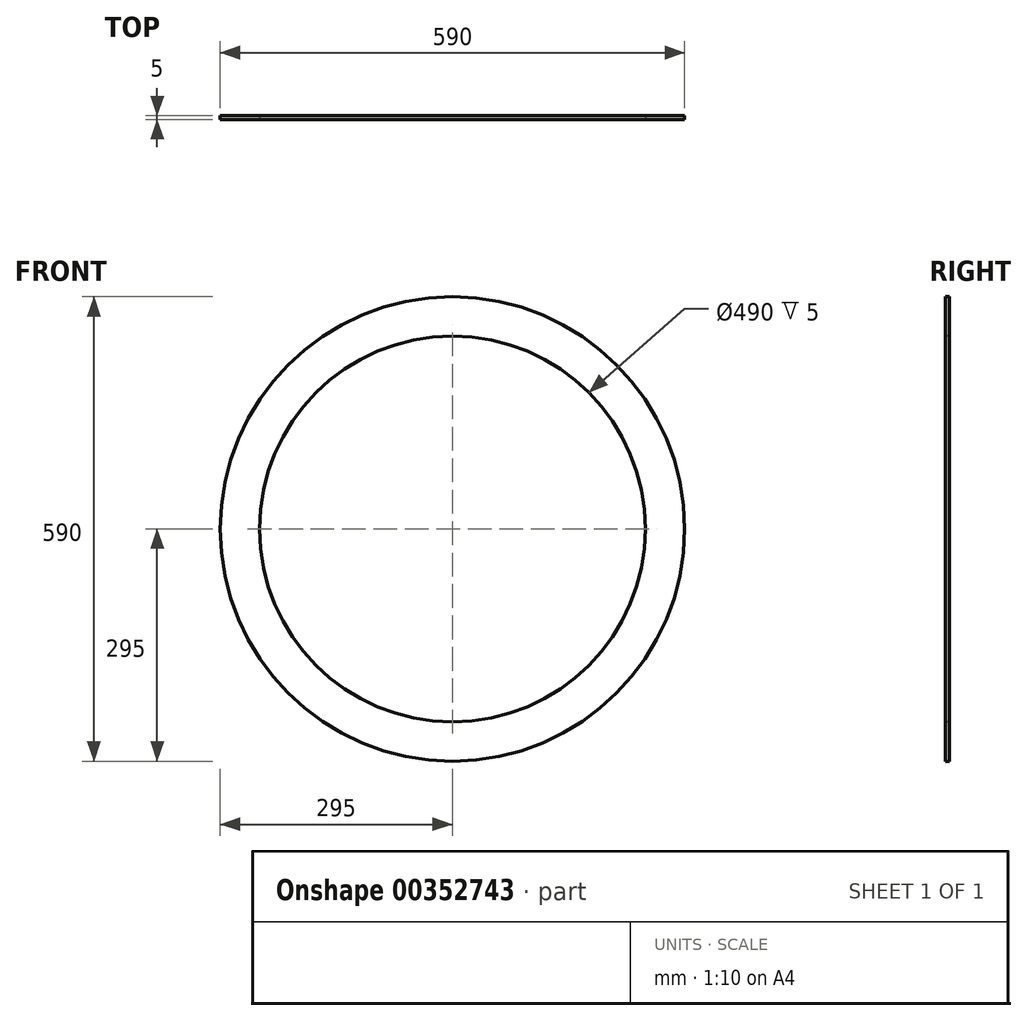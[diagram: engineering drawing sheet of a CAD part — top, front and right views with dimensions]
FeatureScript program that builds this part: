
annotation { "Feature Type Name" : "Feature", "Feature Type Description" : "" }
export const myFeature = defineFeature(function(context is Context, id is Id, definition is map)
    precondition{}
    {
        {
            var Q0;
            Q0=qCreatedBy(makeId("Front.planeOp"),FACE);
            var sketch = newSketch(context, id + "F0", { "sketchPlane" : qUnion([Q0])});
            skCircle(sketch, "E0", {"center": v(0, 0) * mm, "radius": 245 * mm});
            skCircle(sketch, "E1", {"center": v(0, 0) * mm, "radius": 295 * mm});
            skSolve(sketch);
        }
        {
            var Q0;
            Q0=makeQuery(id+"F0.imprint","IMPRINT",FACE,{"disambiguationData":[TD([[makeQuery(id+"F0.imprint","IMPRINT",EDGE,{"derivedFrom":sQuery(id+"F0.wireOp",EDGE,"E0")}),-1.0]])]});
            extrude(context, id + "F1", {"entities" : qUnion([Q0]), "oppositeDirection" : true, "depth" : 5 * mm});
        }
    });
